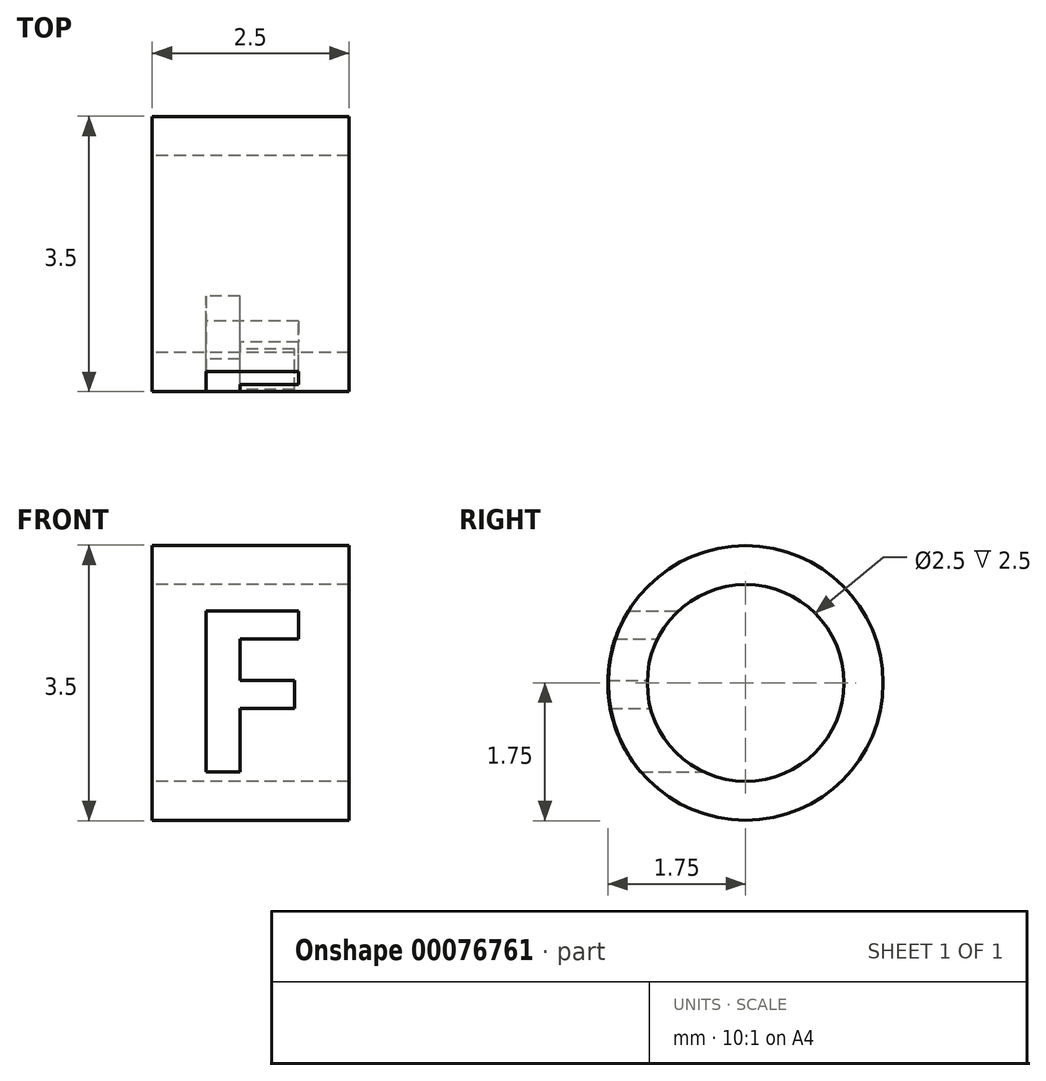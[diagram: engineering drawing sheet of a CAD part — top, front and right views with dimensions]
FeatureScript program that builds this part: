
annotation { "Feature Type Name" : "Feature", "Feature Type Description" : "" }
export const myFeature = defineFeature(function(context is Context, id is Id, definition is map)
    precondition{}
    {
        {
            var Q0;
            Q0=qCreatedBy(makeId("Right.planeOp"),FACE);
            var sketch = newSketch(context, id + "F0", { "sketchPlane" : qUnion([Q0])});
            skCircle(sketch, "E0", {"center": v(0, 0) * mm, "radius": 1.25 * mm});
            skCircle(sketch, "E1", {"center": v(0, 0) * mm, "radius": 1.75 * mm});
            skSolve(sketch);
        }
        {
            var Q0;
            Q0=makeQuery(id+"F0.imprint","IMPRINT",FACE,{"disambiguationData":[TD([[makeQuery(id+"F0.imprint","IMPRINT",EDGE,{"derivedFrom":sQuery(id+"F0.wireOp",EDGE,"E0")}),-1.0]])]});
            var Q1;
            Q1=makeQuery(id+"F0.imprint","IMPRINT",FACE,{"disambiguationData":[TD([[makeQuery(id+"F0.imprint","IMPRINT",EDGE,{"derivedFrom":sQuery(id+"F0.wireOp",EDGE,"E1")}),1.0]])]});
            extrude(context, id + "F1", {"entities" : qUnion([Q0, Q1]), "depth" : 2.5 * mm});
        }
        {
            var Q0;
            Q0=qCreatedBy(makeId("Front.planeOp"),FACE);
            var sketch = newSketch(context, id + "F2", { "sketchPlane" : qUnion([Q0])});
            skText(sketch, "E2", { "text": "F", "fontName": "OpenSans-Bold.ttf"});
            const initialGuessF2  = {"E2": [0.00043, -0.00113, 1, 0, 0.00206]};
            skSetInitialGuess(sketch, initialGuessF2);
            skSolve(sketch);
        }
        {
            var Q0;
            Q0=qSketchRegion(id+"F2",true);
            var Q1;
            Q1=qConstructionFilter(qBodyType(qCreatedBy(id+"F2",EDGE),BodyType.WIRE),ConstructionObject.NO);
            var Q2;
            Q2=makeQuery(id+"F1.opExtrude","SWEPT_FACE",FACE,{"disambiguationData":[OSD([sQuery(id+"F0.wireOp",EDGE,"E1")])]});
            var Q3;
            Q3=makeQuery(id+"F1.opExtrude","SWEPT_BODY",BODY,{"disambiguationData":[OSD([sQuery(id+"F0.wireOp",EDGE,"E0"),sQuery(id+"F0.wireOp",EDGE,"E1")])]});
            var Q4;
            Q4=sQuery(id+"F0.wireOp",VERTEX,"27635d6e-dcd6-4653-b727-4819003c0945");
            extrude(context, id + "F3", {"entities" : qUnion([Q0]), "operationType" : NewBodyOperationType.INTERSECT, "surfaceEntities" : qUnion([Q1]), "endBound" : BoundingType.UP_TO_SURFACE, "endBoundEntityFace" : qUnion([Q2]), "endBoundEntityBody" : qUnion([Q3]), "endBoundEntityVertex" : qUnion([Q4]), "depth" : 25 * mm});
        }
        {
            var Q0;
            Q0=makeQuery(id+"F0.imprint","IMPRINT",FACE,{"disambiguationData":[TD([[makeQuery(id+"F0.imprint","IMPRINT",EDGE,{"derivedFrom":sQuery(id+"F0.wireOp",EDGE,"E0")}),-1.0]])]});
            extrude(context, id + "F4", {"entities" : qUnion([Q0]), "depth" : 2.5 * mm});
        }
    });
